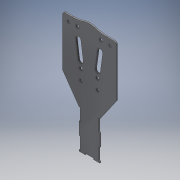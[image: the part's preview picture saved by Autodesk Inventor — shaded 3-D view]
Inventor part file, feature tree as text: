
AUTODESK INVENTOR PART (.ipt)
format: ipt  version: 2017 (Build 210142000, 142)  size: 178,176 bytes
history: native  units: in
note: dims shown in document units (in); Inventor stores cm internally (conversion verified against a paired STEP export)
features: extrude x2, sketch x2
ambient origin geometry x8: Origin, YZ Plane, XZ Plane, XY Plane, X Axis, Y Axis, Z Axis, Center Point
bodies: Solid1 (feature_tree)
feature tree (4):
  extrude  "Extrusion1"  Depth=1.1811in
  extrude  "Extrusion2"  Depth=1.1811in
  sketch  "Sketch1"  dims[d2=0.1181in d3=0.0in d5=1.1811in]
  sketch  "Sketch2"  dims[d6=1.1811in d7=1.1811in d10=0.1181in d11=0.1181in d12=9.4488in d13=1.9685in d14=0.2362in d15=0.0in d16=0.7874in d17=0.1181in]
